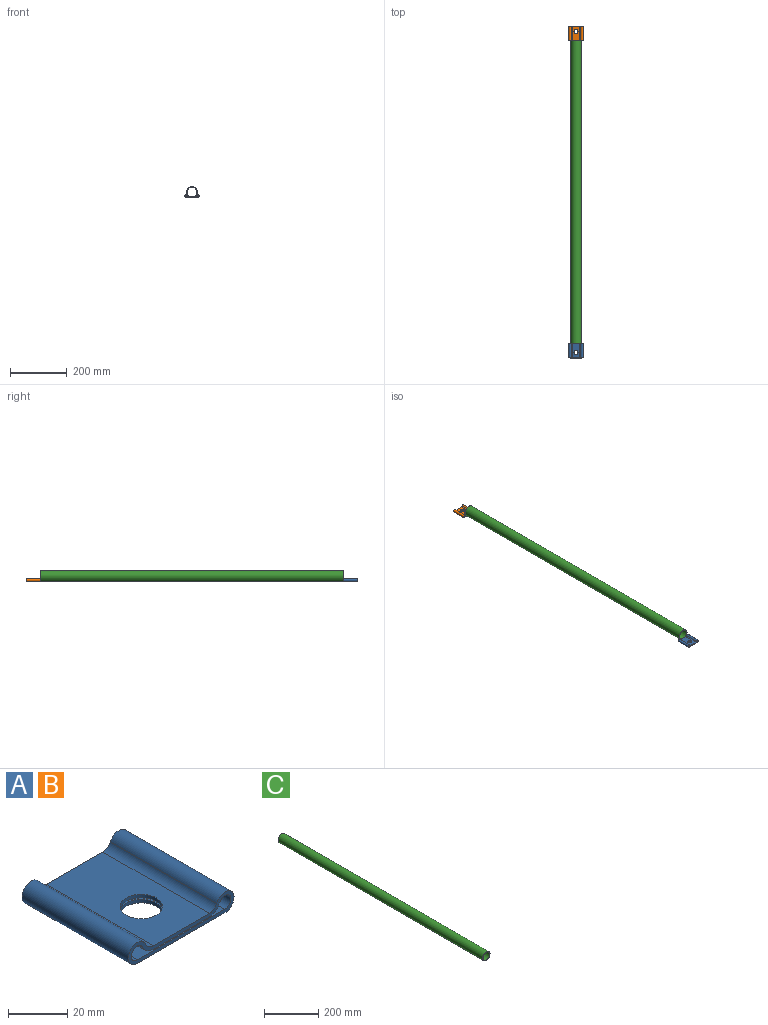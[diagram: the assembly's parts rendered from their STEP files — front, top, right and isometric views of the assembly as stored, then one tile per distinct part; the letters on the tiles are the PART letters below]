
ASSEMBLY  parts=3 mates=2
PART A: 16 faces, bbox 50.5x50.8x8.6 mm
  f0: cylinder r=3.81mm len=50.8mm, axis (0,1,0), area 230.1mm2, adj f1,f11,f12,f13
  f1: cylinder r=4.32mm len=50.8mm, axis (0,1,0), area 949.9mm2, adj f0,f2,f12,f13
  f2: plane 50.8x41.91mm, normal (0,0,-1), area 1968.7mm2, adj f1,f3,f12,f13,f15
  f3: cylinder r=4.32mm len=50.8mm, axis (0,1,0), area 949.9mm2, adj f2,f4,f12,f13
  f4: cylinder r=3.81mm len=50.8mm, axis (0,1,0), area 230.1mm2, adj f3,f11,f12,f13
  f5: plane 50.8x26.83mm, normal (0,0,-1), area 1202.4mm2, adj f6,f10,f12,f13,f14
  f6: cylinder r=5.28mm len=50.8mm, axis (0,1,0), area 319.1mm2, adj f5,f7,f12,f13
  f7: cylinder r=2.84mm len=50.8mm, axis (0,1,0), area 625.8mm2, adj f6,f8,f12,f13
  f8: plane 50.8x41.91mm, normal (0,0,1), area 1968.7mm2, adj f7,f9,f12,f13,f15
  f9: cylinder r=2.84mm len=50.8mm, axis (0,1,0), area 625.8mm2, adj f8,f10,f12,f13
  f10: cylinder r=5.28mm len=50.8mm, axis (0,1,0), area 319.1mm2, adj f5,f9,f12,f13
  f11: plane 50.8x26.83mm, normal (0,0,1), area 1202.4mm2, adj f0,f4,f12,f13,f14
  f12: plane 50.55x8.64mm, normal (0,-1,0), area 162.9mm2, adj f0,f1,f2,f3,f4,f5,f6,f7
  f13: plane 50.55x8.64mm, normal (0,1,0), area 162.9mm2, adj f0,f1,f2,f3,f4,f5,f6,f7
  f14: cylinder r=7.14mm len=14.29mm, axis (0,0,-1), area 66.1mm2, adj f5,f11
  f15: cylinder r=7.14mm len=14.29mm, axis (0,0,-1), area 66.1mm2, adj f2,f8
PART B: same geometry as A
PART C: 4 faces, bbox 38.1x1070.2x38.1 mm
  f0: cylinder r=17.4mm len=1070.23mm, axis (0,1,0), area 116998.7mm2, adj f2,f3
  f1: cylinder r=19.05mm len=1070.23mm, axis (0,1,0), area 128100.7mm2, adj f2,f3
  f2: plane 38.1x38.1mm, normal (0,-1,0), area 189.1mm2, adj f0,f1
  f3: plane 38.1x38.1mm, normal (0,1,0), area 189.1mm2, adj f0,f1
PLACE A t=(45.71,-336.3,-15.54)mm
PLACE B rot(axis=(0,0,1),180deg) t=(45.71,733.93,-15.54)mm
PLACE C t=(45.71,198.81,-15.54)mm
MATE fastened A.f13 <-> C.f2  axis (0,1,0) through (45.71,-336.3,-15.54)mm
MATE fastened B.f13 <-> C.f3  axis (0,-1,0) through (45.71,733.93,-15.54)mm
